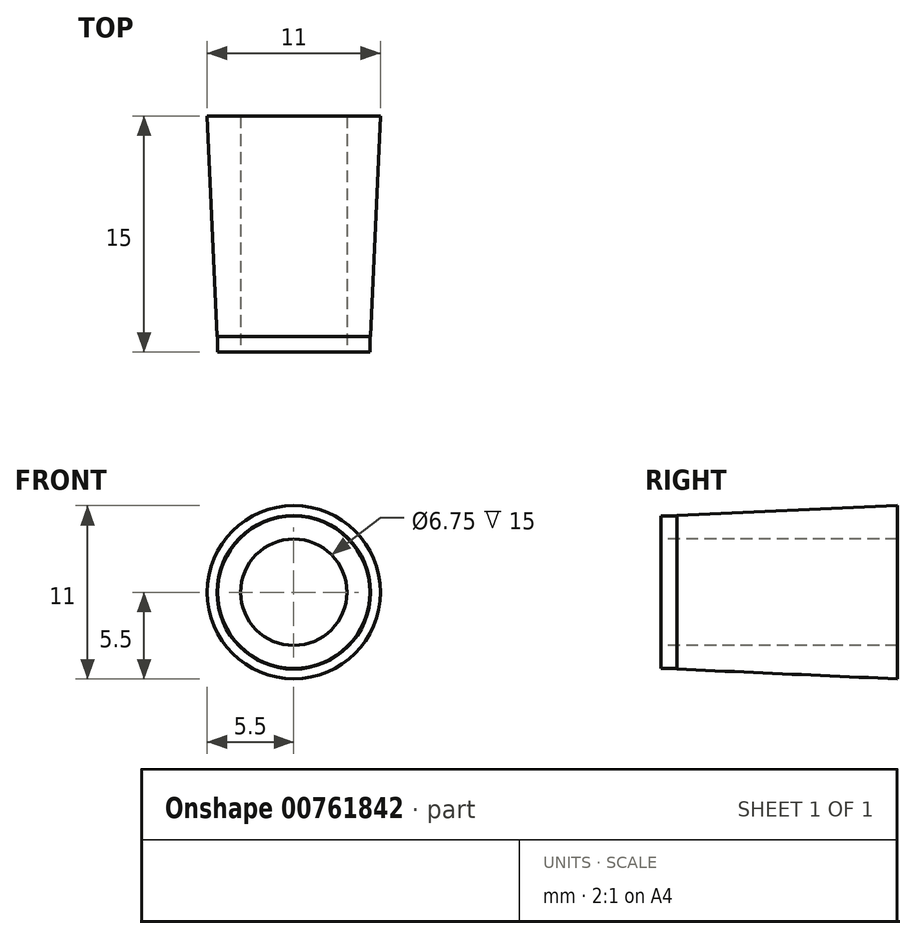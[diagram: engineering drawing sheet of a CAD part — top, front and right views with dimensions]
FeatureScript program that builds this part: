
annotation { "Feature Type Name" : "Feature", "Feature Type Description" : "" }
export const myFeature = defineFeature(function(context is Context, id is Id, definition is map)
    precondition{}
    {
        {
            var Q0;
            Q0=qCreatedBy(makeId("Front.planeOp"),FACE);
            var sketch = newSketch(context, id + "F0", { "sketchPlane" : qUnion([Q0])});
            skCircle(sketch, "E0", {"center": v(0, 0) * mm, "radius": 5.5 * mm});
            skSolve(sketch);
        }
        {
            var Q0;
            Q0=qCreatedBy(makeId("Front.planeOp"),FACE);
            var sketch = newSketch(context, id + "F1", { "sketchPlane" : qUnion([Q0])});
            skCircle(sketch, "E1", {"center": v(0, 0) * mm, "radius": 4.83 * mm});
            skSolve(sketch);
        }
        {
            var Q0;
            Q0=makeQuery(id+"F0.imprint","IMPRINT",FACE,{"disambiguationData":[TD([[makeQuery(id+"F0.imprint","IMPRINT",EDGE,{"derivedFrom":sQuery(id+"F0.wireOp",EDGE,"E0")}),1.0]])]});
            extrude(context, id + "F2", {"entities" : qUnion([Q0]), "depth" : 14 * mm, "offsetDistance" : 25 * mm});
        }
        {
            var Q0;
            Q0=makeQuery(id+"F1.imprint","IMPRINT",FACE,{"disambiguationData":[TD([[makeQuery(id+"F1.imprint","IMPRINT",EDGE,{"derivedFrom":sQuery(id+"F1.wireOp",EDGE,"E1")}),1.0]])]});
            extrude(context, id + "F3", {"entities" : qUnion([Q0]), "operationType" : NewBodyOperationType.ADD, "depth" : 15 * mm, "offsetDistance" : 25 * mm});
        }
        {
            var Q1;
            Q1=makeQuery(id+"F3.opExtrude","CAP_FACE",FACE,{"disambiguationData":[OSD([sQuery(id+"F1.wireOp",EDGE,"E1")])],"isStart":false});
            var Q2;
            Q2=makeQuery(id+"F2.opExtrude","CAP_FACE",FACE,{"disambiguationData":[OSD([sQuery(id+"F0.wireOp",EDGE,"E0")])],"isStart":true});
            loft(context, id + "F4", {"operationType" : NewBodyOperationType.INTERSECT, "sheetProfilesArray" : [{ "sheetProfileEntities" : qUnion([Q1]) }, { "sheetProfileEntities" : qUnion([Q2]) }]});
        }
        {
            var Q0;
            Q0=makeQuery(id+"F3.opExtrude","CAP_FACE",FACE,{"disambiguationData":[OSD([sQuery(id+"F1.wireOp",EDGE,"E1")])],"isStart":false});
            var sketch = newSketch(context, id + "F5", { "sketchPlane" : qUnion([Q0])});
            skCircle(sketch, "E2", {"center": v(0, 0) * mm, "radius": 3.37 * mm});
            skSolve(sketch);
        }
        {
            var Q0;
            Q0=makeQuery(id+"F5.imprint","IMPRINT",FACE,{"disambiguationData":[TD([[makeQuery(id+"F5.imprint","IMPRINT",EDGE,{"derivedFrom":sQuery(id+"F5.wireOp",EDGE,"E2")}),1.0]])]});
            extrude(context, id + "F6", {"entities" : qUnion([Q0]), "operationType" : NewBodyOperationType.REMOVE, "oppositeDirection" : true, "depth" : 16 * mm, "offsetDistance" : 25 * mm});
        }
    });
